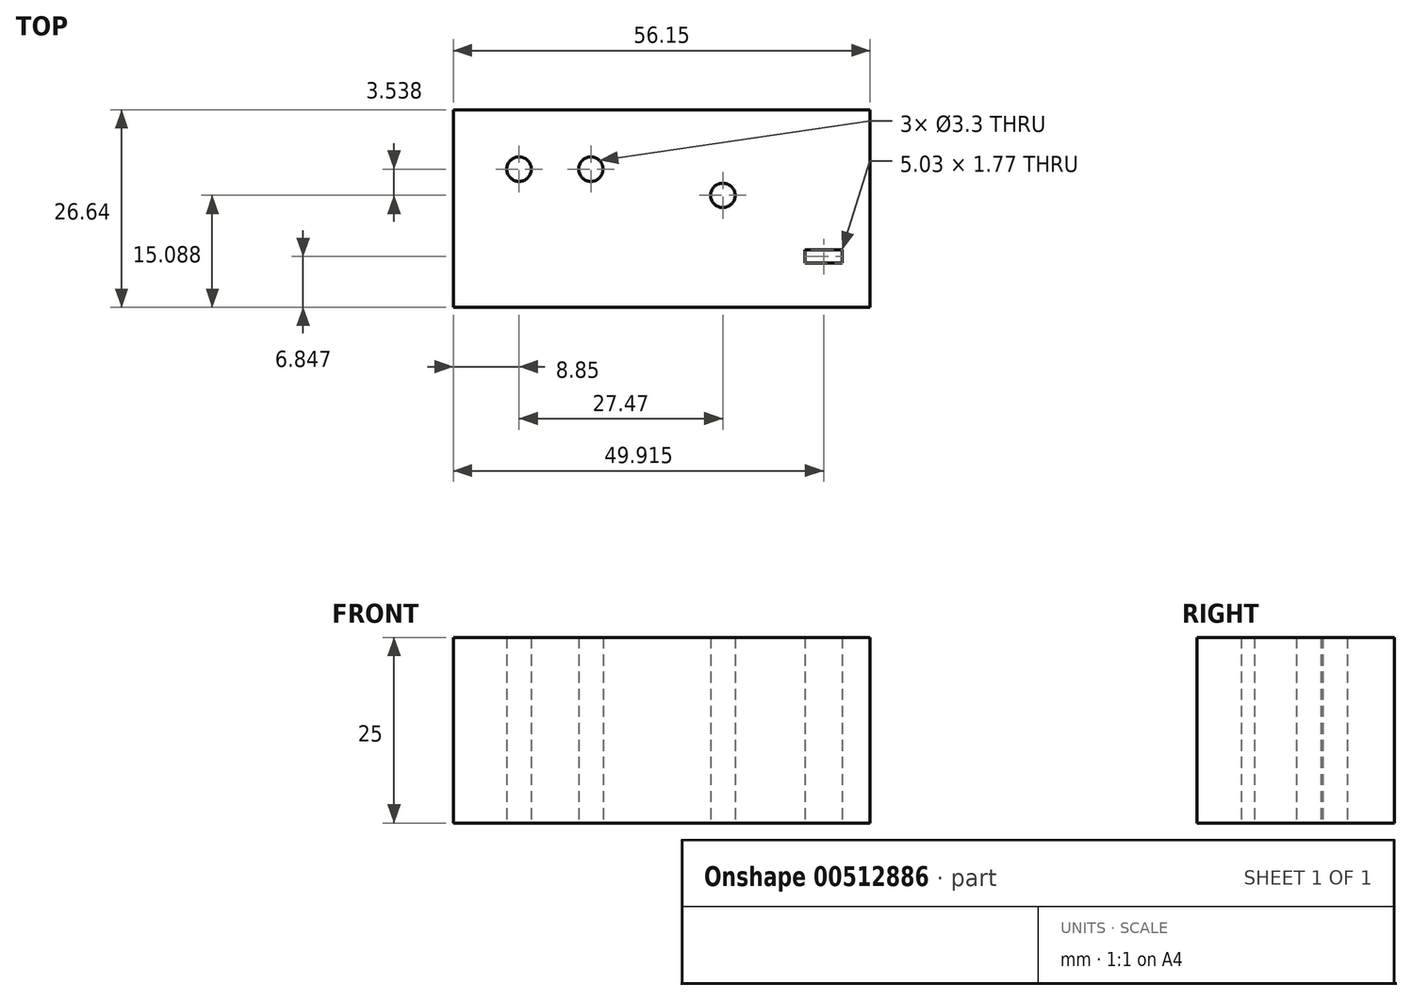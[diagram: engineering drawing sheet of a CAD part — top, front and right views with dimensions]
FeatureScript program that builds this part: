
annotation { "Feature Type Name" : "Feature", "Feature Type Description" : "" }
export const myFeature = defineFeature(function(context is Context, id is Id, definition is map)
    precondition{}
    {
        {
            var Q0;
            Q0=qCreatedBy(makeId("Top.planeOp"),FACE);
            var sketch = newSketch(context, id + "F0", { "sketchPlane" : qUnion([Q0])});
            skPoint(sketch, "E0", {"position": v(-63.27, 8.57) * mm});
            skPoint(sketch, "E1", {"position": v(-72.95, 8.57) * mm});
            skPoint(sketch, "E2", {"position": v(-45.48, 5.03) * mm});
            skSolve(sketch);
        }
        {
            var Q0;
            Q0=qCreatedBy(makeId("Top.planeOp"),FACE);
            var sketch = newSketch(context, id + "F1", { "sketchPlane" : qUnion([Q0])});
            skLineSegment(sketch, "E3.bottom", {"start": v(-81.8, 16.58) * mm, "end": v(-25.65, 16.58) * mm});
            skLineSegment(sketch, "E3.top", {"start": v(-81.8, -10.06) * mm, "end": v(-25.65, -10.06) * mm});
            skLineSegment(sketch, "E3.left", {"start": v(-81.8, 16.58) * mm, "end": v(-81.8, -10.06) * mm});
            skLineSegment(sketch, "E3.right", {"start": v(-25.65, 16.58) * mm, "end": v(-25.65, -10.06) * mm});
            skLineSegment(sketch, "E4.bottom", {"start": v(-34.4, -2.33) * mm, "end": v(-29.37, -2.33) * mm});
            skLineSegment(sketch, "E4.top", {"start": v(-34.4, -4.1) * mm, "end": v(-29.37, -4.1) * mm});
            skLineSegment(sketch, "E4.left", {"start": v(-34.4, -2.33) * mm, "end": v(-34.4, -4.1) * mm});
            skLineSegment(sketch, "E4.right", {"start": v(-29.37, -2.33) * mm, "end": v(-29.37, -4.1) * mm});
            skSolve(sketch);
        }
        {
            var Q0;
            Q0=makeQuery(id+"F1.imprint","IMPRINT",FACE,{"disambiguationData":[TD([[makeQuery(id+"F1.imprint","IMPRINT",EDGE,{"derivedFrom":sQuery(id+"F1.wireOp",EDGE,"E3.bottom")}),-1.0]])]});
            extrude(context, id + "F2", {"entities" : qUnion([Q0]), "depth" : 25 * mm});
        }
        {
            var Q0;
            Q0=sQuery(id+"F0.wireOp",VERTEX,"E1");
            var Q1;
            Q1=sQuery(id+"F0.wireOp",VERTEX,"E0");
            var Q2;
            Q2=sQuery(id+"F0.wireOp",VERTEX,"E2");
            var Q3;
            Q3=makeQuery(id+"F2.opExtrude","SWEPT_BODY",BODY,{"disambiguationData":[OSD([sQuery(id+"F1.wireOp",EDGE,"E3.bottom"),sQuery(id+"F1.wireOp",EDGE,"E3.top"),sQuery(id+"F1.wireOp",EDGE,"E3.left"),sQuery(id+"F1.wireOp",EDGE,"E3.right"),sQuery(id+"F1.wireOp",EDGE,"E4.bottom"),sQuery(id+"F1.wireOp",EDGE,"E4.top"),sQuery(id+"F1.wireOp",EDGE,"E4.left"),sQuery(id+"F1.wireOp",EDGE,"E4.right")])]});
            hole(context, id + "F3", {"style" : HoleStyle.SIMPLE, "endStyle" : HoleEndStyle.BLIND, "oppositeDirection" : true, "holeDiameter" : 3.3 * mm, "holeDepth" : 40 * mm, "isTappedThrough" : true, "tappedDepth" : 12 * mm, "tapClearance" : 3, "locations" : qUnion([Q0, Q1, Q2]), "scope" : qUnion([Q3])});
        }
    });
